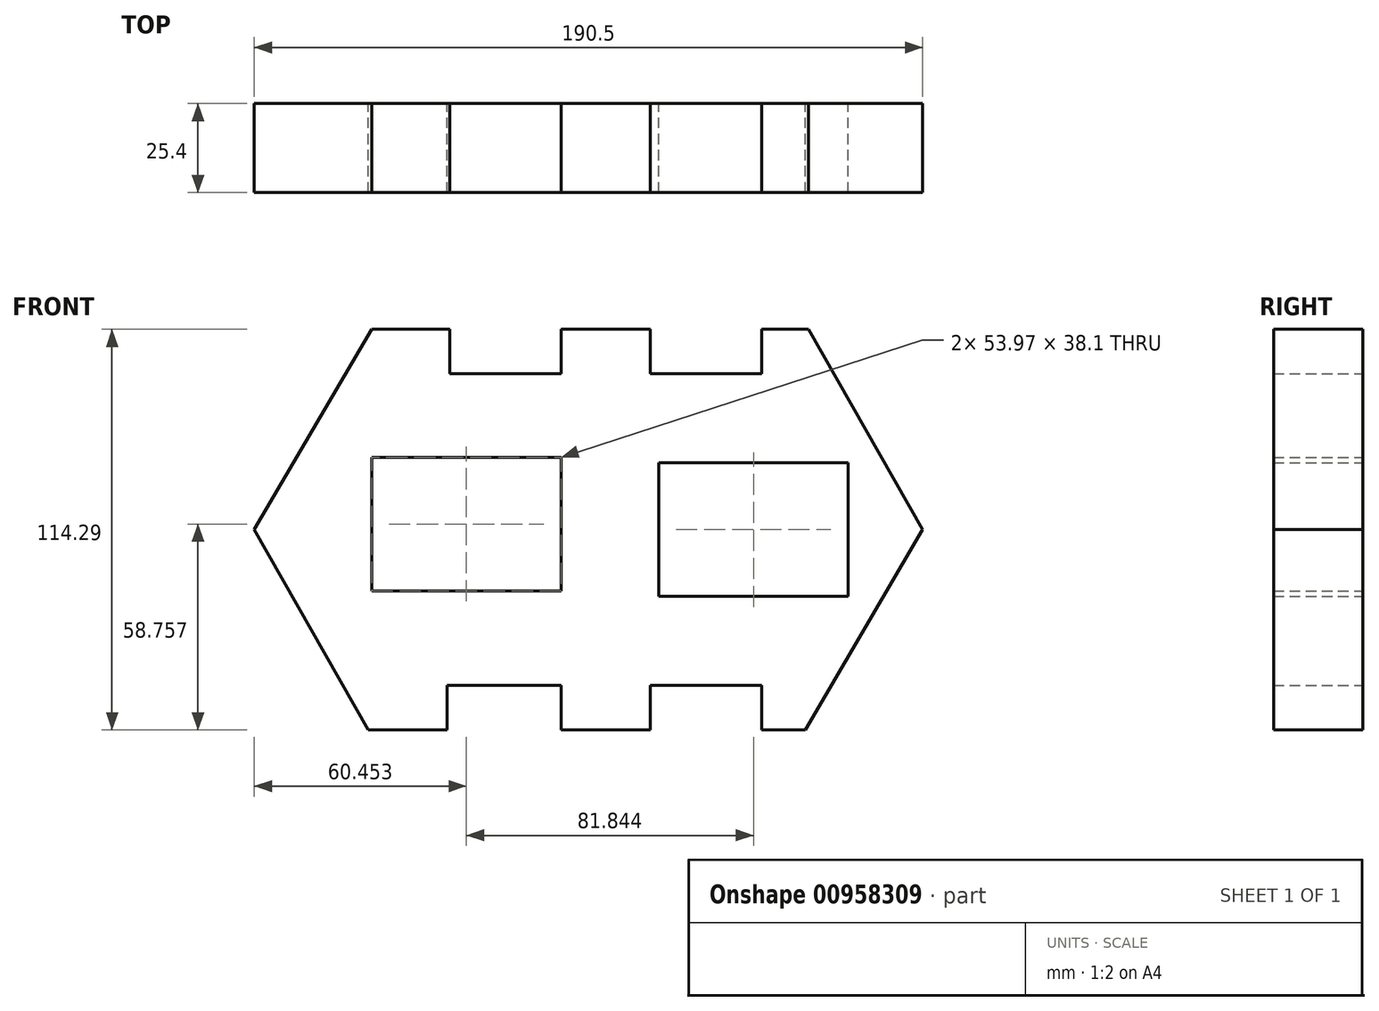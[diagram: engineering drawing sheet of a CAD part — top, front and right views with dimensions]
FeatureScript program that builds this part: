
annotation { "Feature Type Name" : "Feature", "Feature Type Description" : "" }
export const myFeature = defineFeature(function(context is Context, id is Id, definition is map)
    precondition{}
    {
        {
            var Q0;
            Q0=qCreatedBy(makeId("Front.planeOp"),FACE);
            var sketch = newSketch(context, id + "F0", { "sketchPlane" : qUnion([Q0])});
            skLineSegment(sketch, "E0", {"start": v(-63.44, 60.34) * mm, "end": v(-41.22, 60.34) * mm});
            skLineSegment(sketch, "E1", {"start": v(-64.39, -53.95) * mm, "end": v(-41.96, -53.95) * mm});
            skLineSegment(sketch, "E2", {"start": v(-96.91, 3.2) * mm, "end": v(-64.39, -53.95) * mm});
            skLineSegment(sketch, "E3", {"start": v(93.59, 3.2) * mm, "end": v(60.12, -53.95) * mm});
            skLineSegment(sketch, "E4", {"start": v(93.59, 3.2) * mm, "end": v(61.06, 60.34) * mm});
            skLineSegment(sketch, "E5", {"start": v(-96.91, 3.2) * mm, "end": v(-64.46, 58.6) * mm});
            skLineSegment(sketch, "E6", {"start": v(-64.46, 58.6) * mm, "end": v(-63.44, 60.34) * mm});
            skLineSegment(sketch, "E7", {"start": v(-9.47, 60.34) * mm, "end": v(15.93, 60.34) * mm});
            skLineSegment(sketch, "E8", {"start": v(15.93, 60.34) * mm, "end": v(15.93, 47.64) * mm});
            skLineSegment(sketch, "E9", {"start": v(47.68, 60.34) * mm, "end": v(47.68, 47.64) * mm});
            skLineSegment(sketch, "E10", {"start": v(15.93, 47.64) * mm, "end": v(47.68, 47.64) * mm});
            skLineSegment(sketch, "E11", {"start": v(-41.22, 60.34) * mm, "end": v(-41.22, 47.64) * mm});
            skLineSegment(sketch, "E12", {"start": v(-9.47, 60.34) * mm, "end": v(-9.47, 47.64) * mm});
            skLineSegment(sketch, "E13", {"start": v(-41.22, 47.64) * mm, "end": v(-9.47, 47.64) * mm});
            skLineSegment(sketch, "E14", {"start": v(-9.47, -53.95) * mm, "end": v(15.93, -53.95) * mm});
            skLineSegment(sketch, "E15", {"start": v(15.93, -53.95) * mm, "end": v(15.93, -41.25) * mm});
            skLineSegment(sketch, "E16", {"start": v(-9.47, -53.95) * mm, "end": v(-9.47, -41.25) * mm});
            skLineSegment(sketch, "E17", {"start": v(-41.96, -41.25) * mm, "end": v(-9.47, -41.25) * mm});
            skLineSegment(sketch, "E18", {"start": v(47.74, -42.26) * mm, "end": v(47.68, -41.25) * mm});
            skLineSegment(sketch, "E19", {"start": v(15.93, -41.25) * mm, "end": v(47.68, -41.25) * mm});
            skLineSegment(sketch, "E20", {"start": v(-41.96, -41.25) * mm, "end": v(-41.96, -53.95) * mm});
            skLineSegment(sketch, "E21", {"start": v(47.68, -41.25) * mm, "end": v(47.68, -53.95) * mm});
            skLineSegment(sketch, "E22.bottom", {"start": v(199.85, 9.54) * mm, "end": v(199.85, 9.54) * mm});
            skLineSegment(sketch, "E22.top", {"start": v(199.85, -28.61) * mm, "end": v(199.85, -28.61) * mm});
            skLineSegment(sketch, "E22.left", {"start": v(199.85, 9.54) * mm, "end": v(199.85, -28.61) * mm});
            skLineSegment(sketch, "E22.right", {"start": v(199.85, 9.54) * mm, "end": v(199.85, -28.61) * mm});
            skLineSegment(sketch, "E23", {"start": v(-53.74, 23.86) * mm, "end": v(-53.74, 22.24) * mm});
            skLineSegment(sketch, "E24", {"start": v(56.9, 22.25) * mm, "end": v(56.9, 22.24) * mm});
            skLineSegment(sketch, "E25.bottom", {"start": v(-9.47, 23.86) * mm, "end": v(-63.44, 23.86) * mm});
            skLineSegment(sketch, "E25.top", {"start": v(-9.47, -14.24) * mm, "end": v(-63.44, -14.24) * mm});
            skLineSegment(sketch, "E25.left", {"start": v(-9.47, 23.86) * mm, "end": v(-9.47, -14.24) * mm});
            skLineSegment(sketch, "E25.right", {"start": v(-63.44, 23.86) * mm, "end": v(-63.44, -14.24) * mm});
            skLineSegment(sketch, "E26.bottom", {"start": v(18.4, 22.25) * mm, "end": v(72.37, 22.25) * mm});
            skLineSegment(sketch, "E26.top", {"start": v(18.4, -15.85) * mm, "end": v(72.37, -15.85) * mm});
            skLineSegment(sketch, "E26.left", {"start": v(18.4, 22.25) * mm, "end": v(18.4, -15.85) * mm});
            skLineSegment(sketch, "E26.right", {"start": v(72.37, 22.25) * mm, "end": v(72.37, -15.85) * mm});
            skLineSegment(sketch, "E27.trimOffspring", {"start": v(47.68, -53.95) * mm, "end": v(60.12, -53.95) * mm});
            skLineSegment(sketch, "E28.trimOffspring", {"start": v(47.68, 60.34) * mm, "end": v(61.06, 60.34) * mm});
            skPoint(sketch, "E29.orphan", {"position": v(-53.74, 60.34) * mm});
            skPoint(sketch, "E30.orphan", {"position": v(56.9, 60.34) * mm});
            skPoint(sketch, "E31.end.orphan", {"position": v(56.9, -15.85) * mm});
            skPoint(sketch, "E32.end.orphan", {"position": v(-53.74, -15.85) * mm});
            skSolve(sketch);
        }
        {
            var Q0;
            Q0 = qSketchRegion(id + "F0", true);
            extrude(context, id + "F1", {"entities" : qUnion([Q0]), "depth" : 25.4 * mm, "offsetDistance" : 25.4 * mm});
        }
    });
